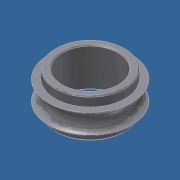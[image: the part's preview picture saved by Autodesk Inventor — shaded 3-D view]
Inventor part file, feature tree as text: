
AUTODESK INVENTOR PART (.ipt)
format: ipt  version: unknown  size: 260,096 bytes
history: native  units: in
note: dims shown in document units (in); Inventor stores cm internally (conversion verified against a paired STEP export)
features: chamfer x2, revolve x1, sketch x1
ambient origin geometry x8: Origin, YZ Plane, XZ Plane, XY Plane, X Axis, Y Axis, Z Axis, Center Point
bodies: Solid1 (feature_tree)
feature tree (4):
  revolve  "Revolution1"  [1 undecoded]
  chamfer  "Chamfer1"  Distance=0.0625in
  chamfer  "Chamfer2"  Distance=0.18in
  sketch  "Sketch1"  dims[d0=0.0856in d2=0.0856in d3=0.0625in d7=0.18in d8=0.003in d9=90.0deg d10=0.01in d11=0.125in d12=45.0deg d13=0.01in d14=0.125in d15=45.0deg d16=0.1875in d20=0.1236in d21=0.1565in]
note: 1 required parameter value undecoded (feature->parameter linkage not recoverable at this tier; creation-order binding heuristic only, values carry confidence <= 0.55)
